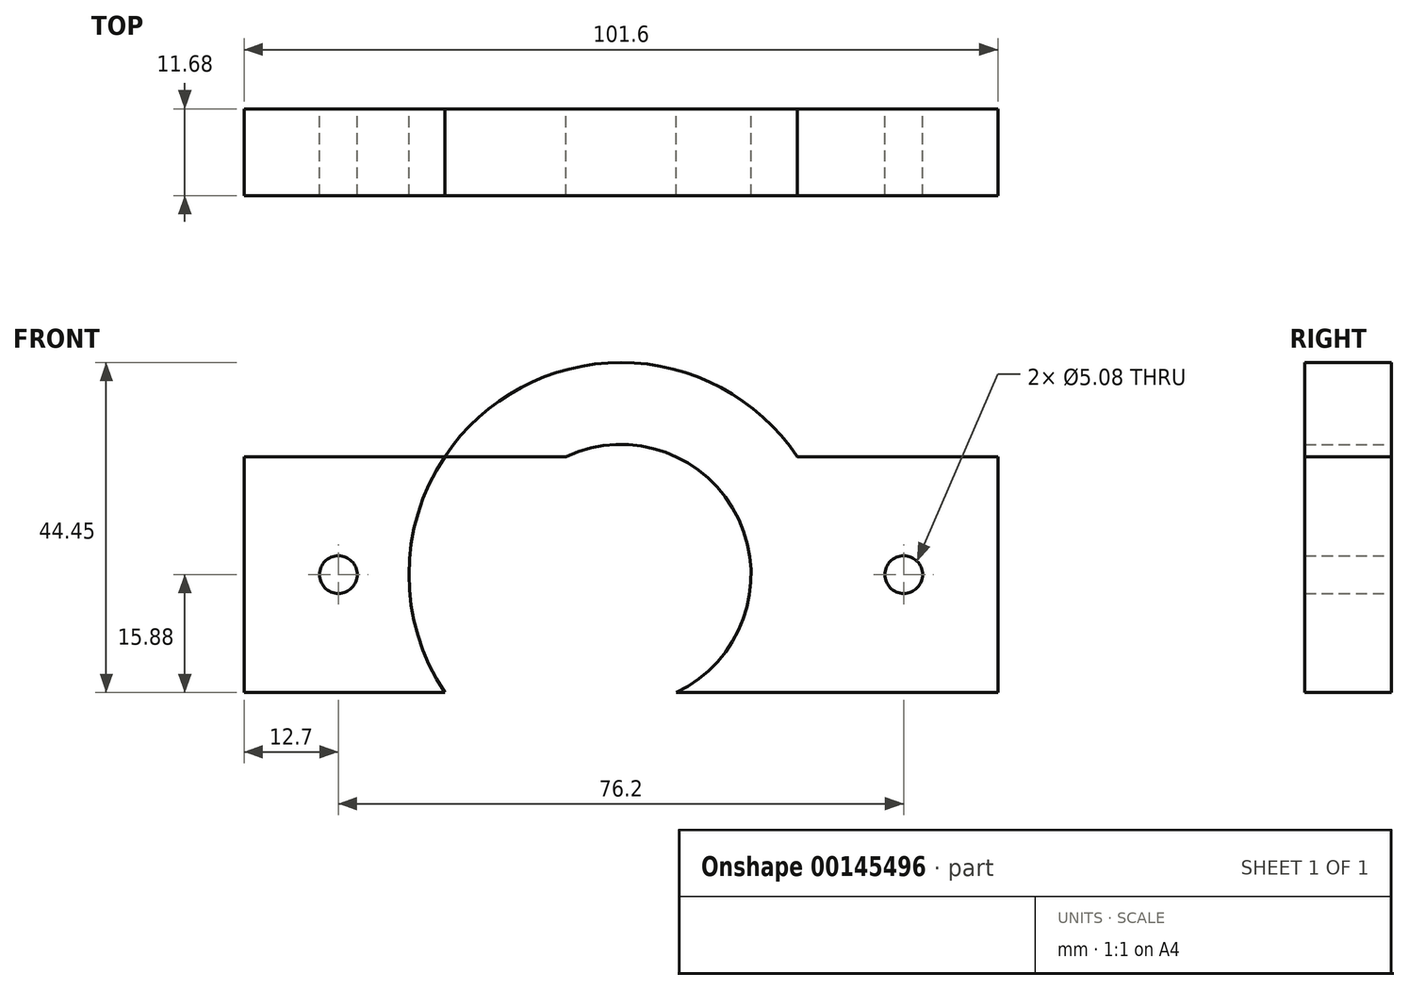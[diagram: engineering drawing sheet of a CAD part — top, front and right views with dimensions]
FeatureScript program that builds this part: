
annotation { "Feature Type Name" : "Feature", "Feature Type Description" : "" }
export const myFeature = defineFeature(function(context is Context, id is Id, definition is map)
    precondition{}
    {
        {
            var Q0;
            Q0=qCreatedBy(makeId("Front.planeOp"),FACE);
            var sketch = newSketch(context, id + "F0", { "sketchPlane" : qUnion([Q0])});
            skCircle(sketch, "E0", {"center": v(0, 0) * mm, "radius": 17.53 * mm});
            skCircle(sketch, "E1", {"center": v(0, 0) * mm, "radius": 28.58 * mm});
            skLineSegment(sketch, "E2.bottom", {"start": v(-50.8, 15.88) * mm, "end": v(50.8, 15.87) * mm});
            skLineSegment(sketch, "E2.top", {"start": v(-50.8, -15.87) * mm, "end": v(50.8, -15.88) * mm});
            skLineSegment(sketch, "E2.left", {"start": v(-50.8, 15.87) * mm, "end": v(-50.8, -15.87) * mm});
            skLineSegment(sketch, "E2.right", {"start": v(50.8, 15.87) * mm, "end": v(50.8, -15.87) * mm});
            skPoint(sketch, "E3", {"position": v(-50.8, 0) * mm});
            skPoint(sketch, "E4", {"position": v(50.8, 0) * mm});
            skPoint(sketch, "E5", {"position": v(0, 15.87) * mm});
            skPoint(sketch, "E6", {"position": v(0, -15.87) * mm});
            skCircle(sketch, "E7", {"center": v(-38.1, 0) * mm, "radius": 2.54 * mm});
            skCircle(sketch, "E8", {"center": v(38.1, 0) * mm, "radius": 2.54 * mm});
            skSolve(sketch);
        }
        {
            var Q0;
            {var subQ0=sQuery(id+"F0.wireOp",EDGE,"E2.bottom");var subQ1=sQuery(id+"F0.wireOp",EDGE,"E0");var subQ2=makeQuery(id+"F0.imprint","INTERSECT",VERTEX,{"disambiguationData":[OD(0.0)],"derivedFrom":[subQ1,subQ0]});Q0=makeQuery(id+"F0.imprint","IMPRINT",FACE,{"disambiguationData":[TD([[makeQuery(id+"F0.imprint","IMPRINT",EDGE,{"disambiguationData":[TD([[subQ2,1.0]])],"derivedFrom":subQ1}),-1.0]])]});}
            var Q1;
            {var subQ0=sQuery(id+"F0.wireOp",EDGE,"E2.top");var subQ1=sQuery(id+"F0.wireOp",EDGE,"E0");var subQ2=makeQuery(id+"F0.imprint","INTERSECT",VERTEX,{"disambiguationData":[OD(0.0)],"derivedFrom":[subQ1,subQ0]});Q1=makeQuery(id+"F0.imprint","IMPRINT",FACE,{"disambiguationData":[TD([[makeQuery(id+"F0.imprint","IMPRINT",EDGE,{"disambiguationData":[TD([[subQ2,-1.0]])],"derivedFrom":subQ1}),-1.0]])]});}
            var Q2;
            {var subQ0=sQuery(id+"F0.wireOp",EDGE,"E2.bottom");var subQ1=sQuery(id+"F0.wireOp",EDGE,"E0");var subQ2=makeQuery(id+"F0.imprint","INTERSECT",VERTEX,{"disambiguationData":[OD(0.0)],"derivedFrom":[subQ1,subQ0]});Q2=makeQuery(id+"F0.imprint","IMPRINT",FACE,{"disambiguationData":[TD([[makeQuery(id+"F0.imprint","IMPRINT",EDGE,{"disambiguationData":[TD([[subQ2,-1.0]])],"derivedFrom":subQ1}),-1.0]])]});}
            var Q3;
            {var subQ0=sQuery(id+"F0.wireOp",EDGE,"E2.bottom");var subQ1=sQuery(id+"F0.wireOp",EDGE,"E0");var subQ2=makeQuery(id+"F0.imprint","INTERSECT",VERTEX,{"disambiguationData":[OD(1.0)],"derivedFrom":[subQ1,subQ0]});Q3=makeQuery(id+"F0.imprint","IMPRINT",FACE,{"disambiguationData":[TD([[makeQuery(id+"F0.imprint","IMPRINT",EDGE,{"disambiguationData":[TD([[subQ2,1.0]])],"derivedFrom":subQ1}),-1.0]])]});}
            var Q4;
            {var subQ0=sQuery(id+"F0.wireOp",EDGE,"E2.right");Q4=makeQuery(id+"F0.imprint","IMPRINT",FACE,{"disambiguationData":[TD([[makeQuery(id+"F0.imprint","IMPRINT",EDGE,{"derivedFrom":subQ0}),-1.0]])]});}
            var Q5;
            {var subQ0=sQuery(id+"F0.wireOp",EDGE,"E2.left");Q5=makeQuery(id+"F0.imprint","IMPRINT",FACE,{"disambiguationData":[TD([[makeQuery(id+"F0.imprint","IMPRINT",EDGE,{"derivedFrom":subQ0}),1.0]])]});}
            extrude(context, id + "F1", {"entities" : qUnion([Q0, Q1, Q2, Q3, Q4, Q5]), "depth" : 11.68 * mm});
        }
    });
